# Revit family: LAMP_GAP G2 LED
name_source: partatom
category: Modelos genéricos
revit_build: Autodesk Revit 2015 (Build: 20140606_1530(x64)
units: mm (PartAtom-declared; Revit-internal decimal feet)

## types (18) — shared parameters
CRI = 80
Diameter = 270 mm  [stored 0.885827 ft]
Elevación por defecto = 1219 mm
Fabricante = LAMP
Finish = Texturised grey
Gear = Electronic
Height = 109 mm  [stored 0.357612 ft]
IEE = A+
Installation instructions = http://www.lamp.es
Insulation class = I
Lamp = HIGH POWER LED
Last update = 12/02/2019
Luminaire type = OUTDOOR - RECESSED DOWNLIGHT
MacAdam = 3
Manufacturer URL = http://www.lamp.es
Manufacturer country = Spain
Manufacturer name = LAMP
Photometric web file = Cuerpo GAP : 670LM 3000 SPOT
Power Supply = 220-240V 50/60Hz
Product URL = http://www.lamp.es
Product datasheet = http://www.lamp.es
Protection rating = IP67 / IK10
Recessed diameter = 248 mm  [stored 0.813648 ft]
Type = HIGH POWER NICHIA
Weight = 3.80 kg

## per-type parameters (varying)
| type | Descripción | Efficacy | Initial color | Initial intensity | LED Lifetime | Modelo | Plum | Power | Product code |
| 1081LM 3000 MEDIUM FLOOD | GAP G2 1400 WW MFL INOX | 83 lm/W | 3000 K | 1081 lm | 60.000 L90 B10 | GA215MF830NI | 13 W | 10 W | GA215MF830NI |
| 1081LM 4000 MEDIUM FLOOD | GAP G2 1400 NW MFL INOX | 83 lm/W | 4000 K | 1081 lm | 60.000 L90 B10 | GA215MF840NI | 13 W | 10 W | GA215MF840NI |
| 1092LM 3000 WIDE FLOOD | GAP G2 1400 WW WFL INOX | 84 lm/W | 3000 K | 1092 lm | 60.000 L90 B10 | GA215WF830NI | 13 W | 10 W | GA215WF830NI |
| 1092LM 4000 WIDE FLOOD | GAP G2 1400 NW WFL INOX | 84 lm/W | 4000 K | 1092 lm | 60.000 L90 B10 | GA215WF840NI | 13 W | 10 W | GA215WF840NI |
| 1130LM 3000 SPOT | GAP G2 1400 WW SP INOX | 87 lm/W | 3000 K | 1130 lm | 60.000 L90 B10 | GA215SP830NI | 13 W | 10 W | GA215SP830NI |
| 1130LM 4000 SPOT | GAP G2 1400 NW SP INOX | 87 lm/W | 4000 K | 1130 lm | 60.000 L90 B10 | GA215SP840NI | 13 W | 10 W | GA215SP840NI |
| 2113LM 3000 MEDIUM FLOOD | GAP G2 2800 WW MFL INOX | 92 lm/W | 3000 K | 2113 lm | 50.000 L90 B10 | GA230MF830NI | 23 W | 20 W | GA230MF830NI |
| 2113LM 4000 MEDIUM FLOOD | GAP G2 2800 NW MFL INOX | 92 lm/W | 4000 K | 2113 lm | 50.000 L90 B10 | GA230MF840NI | 23 W | 20 W | GA230MF840NI |
| 2124LM 3000 WIDE FLOOD | GAP G2 2800 WW WFL INOX | 92 lm/W | 3000 K | 2124 lm | 50.000 L90 B10 | GA230WF830NI | 23 W | 20 W | GA230WF830NI |
| 2124LM 4000 WIDE FLOOD | GAP G2 2800 NW WFL INOX | 92 lm/W | 4000 K | 2124 lm | 50.000 L90 B10 | GA230WF840NI | 23 W | 20 W | GA230WF840NI |
| 2171LM 3000 SPOT | GAP G2 2800 WW SP INOX | 94 lm/W | 3000 K | 2171 lm | 50.000 L90 B10 | GA230SP830NI | 23 W | 20 W | GA230SP830NI |
| 2171LM 4000 SPOT | GAP G2 2800 NW SP INOX | 94 lm/W | 4000 K | 2171 lm | 50.000 L90 B10 | GA230SP840NI | 23 W | 20 W | GA230SP840NI |
| 2851LM 3000 MEDIUM FLOOD | GAP G2 3600 WW MFL INOX | 85 lm/W | 3000 K | 2851 lm | 60.000 L90 B10 | GA235MF830NI | 34 W | 30 W | GA235MF830NI |
| 2851LM 4000 MEDIUM FLOOD | GAP G2 3600 NW MFL INOX | 85 lm/W | 4000 K | 2851 lm | 60.000 L90 B10 | GA235MF840NI | 34 W | 30 W | GA235MF840NI |
| 2877LM 3000 WIDE FLOOD | GAP G2 3600 WW WFL INOX | 86 lm/W | 3000 K | 2877 lm | 60.000 L90 B10 | GA235WF830NI | 34 W | 30 W | GA235WF830NI |
| 2877LM 4000 WIDE FLOOD | GAP G2 3600 NW WFL INOX | 86 lm/W | 4000 K | 2877 lm | 60.000 L90 B10 | GA235WF840NI | 34 W | 30 W | GA235WF840NI |
| 2944LM 3000 SPOT | GAP G2 3600 WW SP INOX | 88 lm/W | 3000 K | 2944 lm | 60.000 L90 B10 | GA235SP830NI | 34 W | 30 W | GA235SP830NI |
| 2944LM 4000 SPOT | GAP G2 3600 NW SP INOX | 88 lm/W | 4000 K | 2944 lm | 60.000 L90 B10 | GA235SP840NI | 34 W | 30 W | GA235SP840NI |

note: [stored X ft] marks values corroborated as IEEE doubles in the binary element streams (Revit-internal decimal feet)
